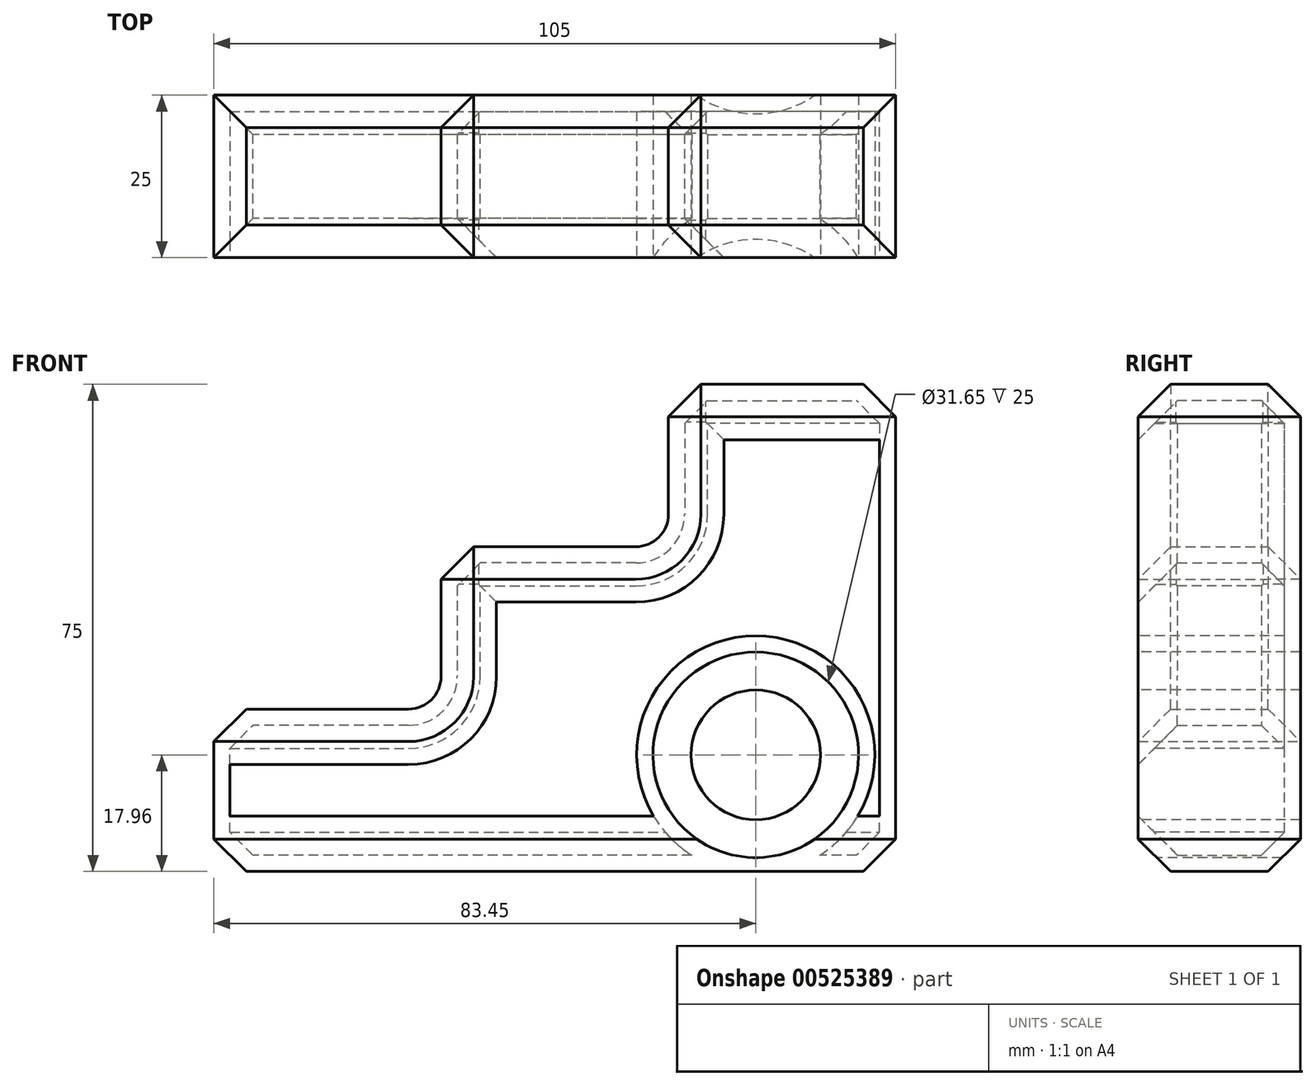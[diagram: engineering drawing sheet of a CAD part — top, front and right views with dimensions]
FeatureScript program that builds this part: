
annotation { "Feature Type Name" : "Feature", "Feature Type Description" : "" }
export const myFeature = defineFeature(function(context is Context, id is Id, definition is map)
    precondition{}
    {
        {
            var Q0;
            Q0=qCreatedBy(makeId("Front.planeOp"),FACE);
            var sketch = newSketch(context, id + "F0", { "sketchPlane" : qUnion([Q0])});
            skLineSegment(sketch, "E0", {"start": v(-46.7, 0) * mm, "end": v(58.3, 0) * mm});
            skLineSegment(sketch, "E1", {"start": v(58.3, 0) * mm, "end": v(58.3, 75) * mm});
            skLineSegment(sketch, "E2", {"start": v(58.3, 75) * mm, "end": v(23.3, 75) * mm});
            skLineSegment(sketch, "E3", {"start": v(-46.7, 0) * mm, "end": v(-46.7, 25) * mm});
            skLineSegment(sketch, "E4", {"start": v(-46.7, 25) * mm, "end": v(-16.7, 25) * mm});
            skLineSegment(sketch, "E5", {"start": v(-11.7, 30) * mm, "end": v(-11.7, 50) * mm});
            skLineSegment(sketch, "E6", {"start": v(-11.7, 50) * mm, "end": v(18.3, 50) * mm});
            skLineSegment(sketch, "E7", {"start": v(23.3, 55) * mm, "end": v(23.3, 75) * mm});
            skPoint(sketch, "E8.visualSharp", {"position": v(-11.7, 25) * mm});
            skArc(sketch, "E8.filletArc", {"start": v(-16.7, 25) * mm, "mid": v(-13.16, 26.46) * mm, "end": v(-11.7, 30) * mm});
            skPoint(sketch, "E9.visualSharp", {"position": v(23.3, 50) * mm});
            skArc(sketch, "E9.filletArc", {"start": v(18.3, 50) * mm, "mid": v(21.84, 51.46) * mm, "end": v(23.3, 55) * mm});
            skSolve(sketch);
        }
        {
            var Q0;
            Q0=makeQuery(id+"F0.imprint","IMPRINT",FACE,{"disambiguationData":[TD([[makeQuery(id+"F0.imprint","IMPRINT",EDGE,{"derivedFrom":sQuery(id+"F0.wireOp",EDGE,"E0")}),1.0]])]});
            extrude(context, id + "F1", {"entities" : qUnion([Q0]), "depth" : 25 * mm, "offsetDistance" : 25 * mm});
        }
        {
            var Q0;
            Q0=makeQuery(id+"F1.opExtrude","CAP_FACE",FACE,{"disambiguationData":[OSD([sQuery(id+"F0.wireOp",EDGE,"E0"),sQuery(id+"F0.wireOp",EDGE,"E1"),sQuery(id+"F0.wireOp",EDGE,"E2"),sQuery(id+"F0.wireOp",EDGE,"E3"),sQuery(id+"F0.wireOp",EDGE,"E4"),sQuery(id+"F0.wireOp",EDGE,"E5"),sQuery(id+"F0.wireOp",EDGE,"E6"),sQuery(id+"F0.wireOp",EDGE,"E7"),sQuery(id+"F0.wireOp",EDGE,"E8.filletArc"),sQuery(id+"F0.wireOp",EDGE,"E9.filletArc")])],"isStart":false});
            var sketch = newSketch(context, id + "F2", { "sketchPlane" : qUnion([Q0])});
            skCircle(sketch, "E10", {"center": v(36.75, 17.96) * mm, "radius": 15.83 * mm});
            skCircle(sketch, "E11", {"center": v(36.75, 17.96) * mm, "radius": 9.98 * mm});
            skSolve(sketch);
        }
        {
            var Q0;
            Q0=makeQuery(id+"F2.imprint","IMPRINT",FACE,{"disambiguationData":[TD([[makeQuery(id+"F2.imprint","IMPRINT",EDGE,{"derivedFrom":sQuery(id+"F2.wireOp",EDGE,"E10")}),1.0]])]});
            extrude(context, id + "F3", {"entities" : qUnion([Q0]), "operationType" : NewBodyOperationType.REMOVE, "oppositeDirection" : true, "depth" : 25 * mm, "offsetDistance" : 25 * mm});
        }
        {
            var Q0;
            Q0=makeQuery(id+"F1.opExtrude","SWEPT_EDGE",EDGE,{"disambiguationData":[OSD([sQuery(id+"F0.wireOp",EDGE,"E3"),sQuery(id+"F0.wireOp",EDGE,"E4")])]});
            var Q1;
            Q1=makeQuery(id+"F1.opExtrude","SWEPT_EDGE",EDGE,{"disambiguationData":[OSD([sQuery(id+"F0.wireOp",EDGE,"E5"),sQuery(id+"F0.wireOp",EDGE,"E6")])]});
            var Q2;
            Q2=makeQuery(id+"F1.opExtrude","SWEPT_EDGE",EDGE,{"disambiguationData":[OSD([sQuery(id+"F0.wireOp",EDGE,"E2"),sQuery(id+"F0.wireOp",EDGE,"E7")])]});
            var Q3;
            Q3=makeQuery(id+"F1.opExtrude","CAP_EDGE",EDGE,{"disambiguationData":[OSD([sQuery(id+"F0.wireOp",EDGE,"E4")])],"isStart":false});
            var Q4;
            Q4=makeQuery(id+"F1.opExtrude","CAP_EDGE",EDGE,{"disambiguationData":[OSD([sQuery(id+"F0.wireOp",EDGE,"E6")])],"isStart":false});
            var Q5;
            Q5=makeQuery(id+"F1.opExtrude","CAP_EDGE",EDGE,{"disambiguationData":[OSD([sQuery(id+"F0.wireOp",EDGE,"E2")])],"isStart":false});
            var Q6;
            Q6=makeQuery(id+"F1.opExtrude","CAP_EDGE",EDGE,{"disambiguationData":[OSD([sQuery(id+"F0.wireOp",EDGE,"E2")])],"isStart":true});
            var Q7;
            Q7=makeQuery(id+"F1.opExtrude","CAP_EDGE",EDGE,{"disambiguationData":[OSD([sQuery(id+"F0.wireOp",EDGE,"E6")])],"isStart":true});
            var Q8;
            Q8=makeQuery(id+"F1.opExtrude","CAP_EDGE",EDGE,{"disambiguationData":[OSD([sQuery(id+"F0.wireOp",EDGE,"E4")])],"isStart":true});
            var Q9;
            Q9=makeQuery(id+"F1.opExtrude","SWEPT_EDGE",EDGE,{"disambiguationData":[OSD([sQuery(id+"F0.wireOp",EDGE,"E1"),sQuery(id+"F0.wireOp",EDGE,"E2")])]});
            var Q10;
            Q10=makeQuery(id+"F1.opExtrude","CAP_EDGE",EDGE,{"disambiguationData":[OSD([sQuery(id+"F0.wireOp",EDGE,"E0")])],"isStart":false});
            var Q11;
            Q11=makeQuery(id+"F1.opExtrude","CAP_EDGE",EDGE,{"disambiguationData":[OSD([sQuery(id+"F0.wireOp",EDGE,"E0")])],"isStart":true});
            var Q12;
            Q12=makeQuery(id+"F1.opExtrude","SWEPT_EDGE",EDGE,{"disambiguationData":[OSD([sQuery(id+"F0.wireOp",EDGE,"E0"),sQuery(id+"F0.wireOp",EDGE,"E3")])]});
            var Q13;
            Q13=makeQuery(id+"F1.opExtrude","SWEPT_EDGE",EDGE,{"disambiguationData":[OSD([sQuery(id+"F0.wireOp",EDGE,"E0"),sQuery(id+"F0.wireOp",EDGE,"E1")])]});
            chamfer(context, id + "F4", {"entities" : qUnion([Q0, Q1, Q2, Q3, Q4, Q5, Q6, Q7, Q8, Q9, Q10, Q11, Q12, Q13]), "width" : 5 * mm, "tangentPropagation" : true});
        }
        {
            var Q0;
            {var subQ0=sQuery(id+"F0.wireOp",EDGE,"E8.filletArc");var subQ1=sQuery(id+"F0.wireOp",EDGE,"E7");var subQ2=sQuery(id+"F0.wireOp",EDGE,"E6");var subQ3=sQuery(id+"F0.wireOp",EDGE,"E5");var subQ4=sQuery(id+"F0.wireOp",EDGE,"E4");var subQ5=sQuery(id+"F0.wireOp",EDGE,"E9.filletArc");var subQ6=sQuery(id+"F0.wireOp",EDGE,"E0");var subQ7=sQuery(id+"F0.wireOp",EDGE,"E3");var subQ8=sQuery(id+"F0.wireOp",EDGE,"E1");var subQ9=sQuery(id+"F0.wireOp",EDGE,"E2");Q0=makeQuery(id+"F3.boolean.opBoolean","SPLIT",FACE,{"disambiguationData":[TD([makeQuery(id+"F1.opExtrude","SWEPT_FACE",FACE,{"disambiguationData":[OSD([subQ6])]})])],"derivedFrom":makeQuery(id+"F1.opExtrude","CAP_FACE",FACE,{"disambiguationData":[OSD([subQ6,subQ8,subQ9,subQ7,subQ4,subQ3,subQ2,subQ1,subQ0,subQ5])],"isStart":false})});}
            shell(context, id + "F5", {"entities" : qUnion([Q0]), "thickness" : 2.5 * mm});
        }
    });
